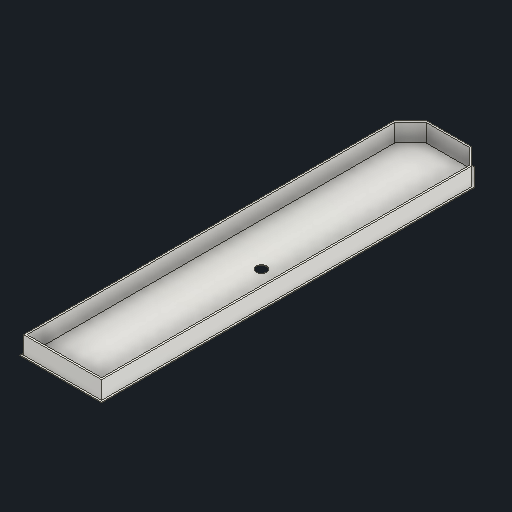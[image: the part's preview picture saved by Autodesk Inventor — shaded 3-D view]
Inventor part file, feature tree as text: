
AUTODESK INVENTOR PART (.ipt)
format: ipt  version: 2022 (Build 260153000, 153)  size: 145,920 bytes
history: native  units: mm
features: other x3, extrude x2, sketch x2, reference x1
ambient origin geometry x8: Origin, YZ Plane, XZ Plane, XY Plane, X Axis, Y Axis, Z Axis, Center Point
bodies: Body1 (feature_tree)
feature tree (8):
  other  "Sólido1"
  extrude  "Extrusión1"  Depth=230.0mm
  extrude  "Extrusion2"  Depth=50.0mm
  sketch  "Boceto1"  dims[d0=1100.0mm d1=230.0mm]
  sketch  "Sketch2"  dims[d2=50.0mm d3=50.0mm d4=50.0mm d5=50.0mm d6=30.0mm d7=100.0mm d10=1.0mm d11=0.0mm d12=30.0mm d13=30.0mm d14=100.0mm d15=275.0mm d16=275.0mm d17=275.0mm d18=100.0mm d19=10.0mm d20=5.0mm d21=50.0mm d22=0.0mm]
  reference  "Reference1"
  other  "Horquilla.iam"
  other  "Horquilla_Cubierta:1"
